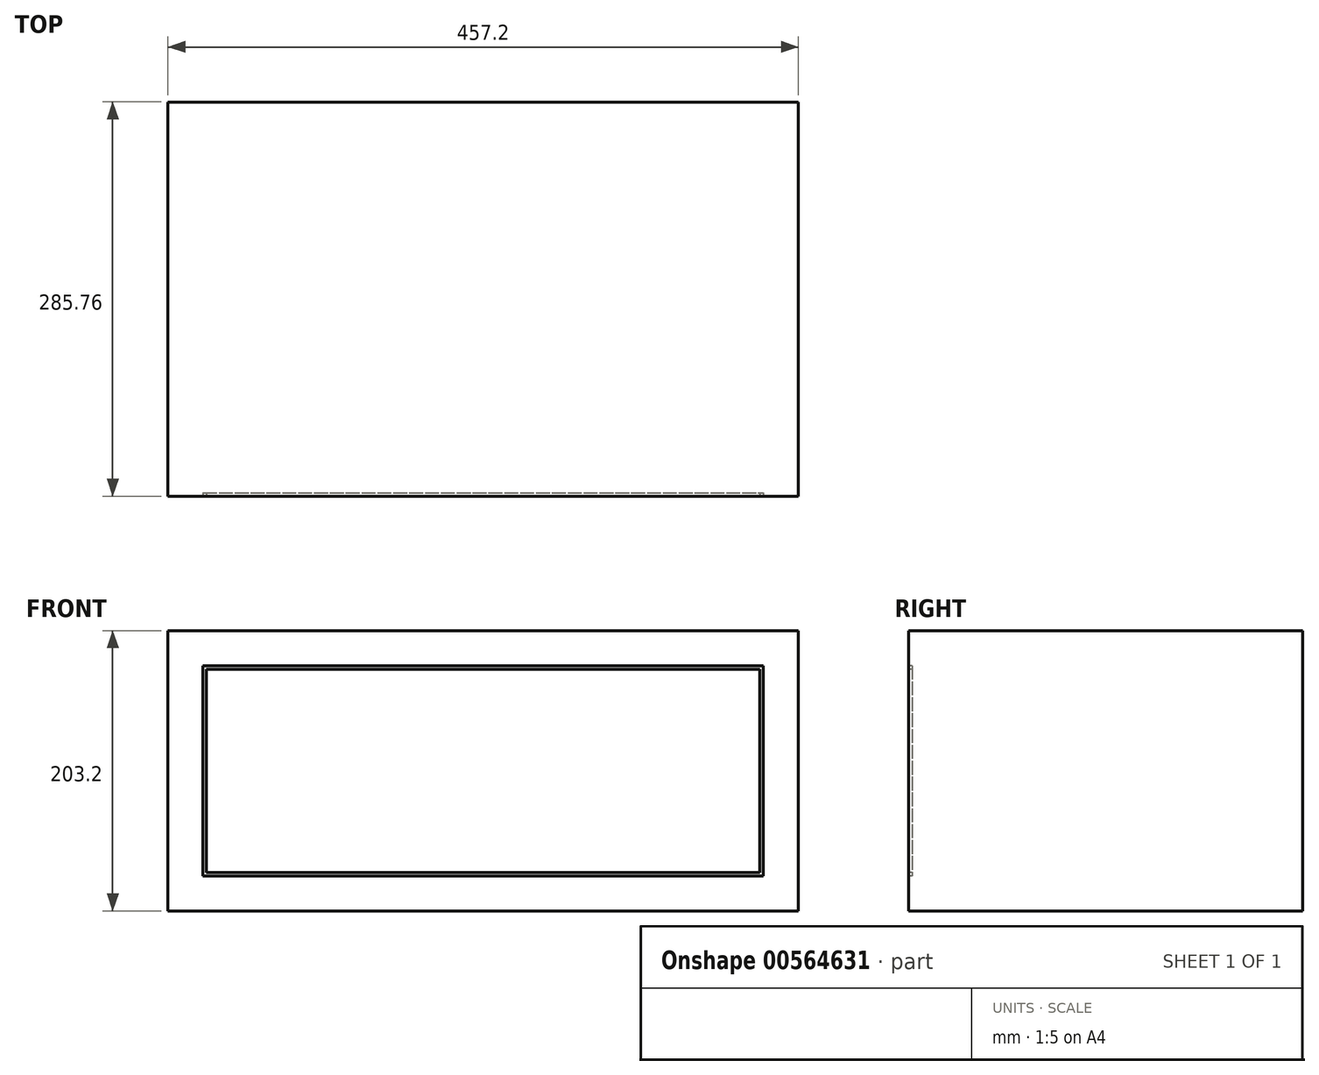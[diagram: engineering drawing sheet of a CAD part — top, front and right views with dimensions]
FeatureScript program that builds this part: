
annotation { "Feature Type Name" : "Feature", "Feature Type Description" : "" }
export const myFeature = defineFeature(function(context is Context, id is Id, definition is map)
    precondition{}
    {
        {
            var Q0;
            Q0=qCreatedBy(makeId("Top.planeOp"),FACE);
            var sketch = newSketch(context, id + "F0", { "sketchPlane" : qUnion([Q0])});
            skLineSegment(sketch, "E0.bottom", {"start": v(-228.6, 142.88) * mm, "end": v(228.6, 142.88) * mm});
            skLineSegment(sketch, "E0.top", {"start": v(-228.6, -142.88) * mm, "end": v(228.6, -142.88) * mm});
            skLineSegment(sketch, "E0.left", {"start": v(-228.6, 142.88) * mm, "end": v(-228.6, -142.87) * mm});
            skLineSegment(sketch, "E0.right", {"start": v(228.6, 142.88) * mm, "end": v(228.6, -142.87) * mm});
            skPoint(sketch, "E0.middle", {"position": v(0, 0) * mm});
            skSolve(sketch);
        }
        {
            var Q0;
            Q0=makeQuery(id+"F0.imprint","IMPRINT",FACE,{"disambiguationData":[TD([[makeQuery(id+"F0.imprint","IMPRINT",EDGE,{"derivedFrom":sQuery(id+"F0.wireOp",EDGE,"E0.bottom")}),-1.0]])]});
            extrude(context, id + "F1", {"entities" : qUnion([Q0]), "depth" : 203.2 * mm, "offsetDistance" : 25.4 * mm});
        }
        {
            var Q0;
            Q0=makeQuery(id+"F1.opExtrude","SWEPT_FACE",FACE,{"disambiguationData":[OSD([sQuery(id+"F0.wireOp",EDGE,"E0.top")])]});
            var sketch = newSketch(context, id + "F2", { "sketchPlane" : qUnion([Q0])});
            skLineSegment(sketch, "E1.bottom", {"start": v(-203.2, 177.8) * mm, "end": v(203.2, 177.8) * mm});
            skLineSegment(sketch, "E1.top", {"start": v(-203.2, 25.4) * mm, "end": v(203.2, 25.4) * mm});
            skLineSegment(sketch, "E1.left", {"start": v(-203.2, 177.8) * mm, "end": v(-203.2, 25.4) * mm});
            skLineSegment(sketch, "E1.right", {"start": v(203.2, 177.8) * mm, "end": v(203.2, 25.4) * mm});
            skPoint(sketch, "E1.middle", {"position": v(0, 101.6) * mm});
            skLineSegment(sketch, "E2.bottom", {"start": v(-200.66, 175.26) * mm, "end": v(200.66, 175.26) * mm});
            skLineSegment(sketch, "E2.top", {"start": v(-200.66, 27.94) * mm, "end": v(200.66, 27.94) * mm});
            skLineSegment(sketch, "E2.left", {"start": v(-200.66, 175.26) * mm, "end": v(-200.66, 27.94) * mm});
            skLineSegment(sketch, "E2.right", {"start": v(200.66, 175.26) * mm, "end": v(200.66, 27.94) * mm});
            skSolve(sketch);
        }
        {
            var Q0;
            Q0 = qSketchRegion(id + "F2", true);
            extrude(context, id + "F3", {"entities" : qUnion([Q0]), "operationType" : NewBodyOperationType.REMOVE, "oppositeDirection" : true, "depth" : 2.54 * mm, "offsetDistance" : 25.4 * mm});
        }
    });
